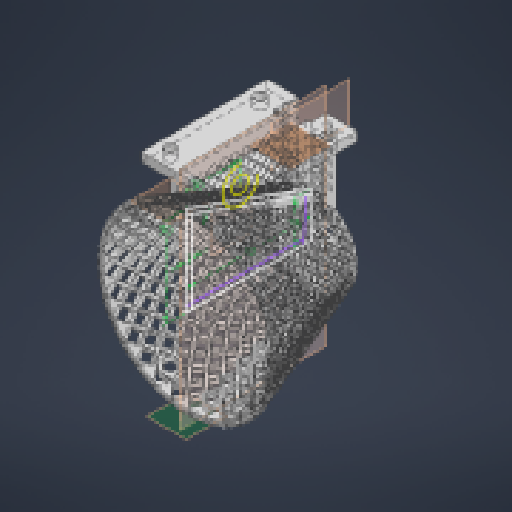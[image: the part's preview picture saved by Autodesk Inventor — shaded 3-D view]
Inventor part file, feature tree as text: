
AUTODESK INVENTOR PART (.ipt)
format: ipt  version: 2025 (Build 290162000, 162)  size: 3,707,392 bytes
history: native  units: mm
features: extrude x12, sketch x10, plane x9, other x9, reference x3, projected_geometry x2, pattern_circular x1, fillet x1
ambient origin geometry x8: Origin, YZ Plane, XZ Plane, XY Plane, X Axis, Y Axis, Z Axis, Center Point
bodies: Solid1 (feature_tree)
feature tree (47):
  plane  "Work Plane1"
  other  "hoop revolution"
  extrude  "net holes"  Depth=25.0mm
  pattern_circular  "Circular Pattern3"  Count=3  [1 undecoded]
  plane  "Work Plane15"
  extrude  "hoop slot"  TaperAngle=90.0deg  [1 undecoded]
  plane  "Work Plane10"
  extrude  "slot walls"  Depth=3.0mm
  plane  "Work Plane12"
  extrude  "arm holes"  Depth=1.0mm
  plane  "Work Plane11"
  sketch  "Sketch19"  dims[d392=1.0mm d393=1.0mm]
  plane  "Work Plane13"
  extrude  "mount holes extrusion"  Depth=1.0mm
  plane  "Work Plane16"
  extrude  "mounting holes and access holes"  Depth=1.0mm
  plane  "Work Plane18"
  extrude  "Extrusion13"  Depth=1.0mm
  plane  "Work Plane21"
  extrude  "back net reinforcement"  Depth=1.0mm
  fillet  "Fillet1"  Radius=1.0mm
  other  "middle plane for part"
  extrude  "Extrusion16"  Depth=1.0mm
  extrude  "Extrusion17"  Depth=10.0mm
  extrude  "Extrusion18"  Depth=10.0mm
  extrude  "Diameter Increase For Ball Clearance"  TaperAngle=0.0deg  [1 undecoded]
  other  "Work Axis1"
  reference  "Reference1"
  reference  "Reference2"
  reference  "Reference3"
  other  "best net sketch"
  projected_geometry  "Projected Loop3"
  sketch  "Sketch16"  dims[d387=1.0mm d388=1.0mm]
  sketch  "Sketch17"  dims[d389=1.0mm d390=1.0mm d391=1.0mm]
  projected_geometry  "Projected Loop4"
  sketch  "Sketch22"  dims[d394=1.0mm d395=1.0mm d396=1.0mm d397=0.0mm d398=0.0mm d399=3.572329mm d400=0.0mm d401=300.0mm d402=360.0deg d404=10.0mm d406=20.0mm d407=0.0mm d408=1.0mm d409=18.099mm d410=0.0mm d411=1.0mm d412=3.0mm d413=50.0mm d414=0.0mm d417=10.0mm d418=0.0mm d419=0.0mm d420=55.0mm d423=3.0mm d424=4.5mm d426=10.0mm d431=5.0mm d432=0.0mm d433=6.0mm d434=6.0mm d439=10.0mm d440=10.0mm d441=6.2mm d442=20.0mm d444=50.0mm d445=20.0mm d447=38.0mm d450=0.0mm d451=0.0mm d452=10.0mm d453=10.0mm d454=10.0mm d455=0.0mm d456=10.0mm d457=10.0mm d458=10.0mm d459=10.0mm d460=10.0mm d461=10.0mm d462=10.0mm d463=0.0mm d464=12.277724mm d465=12.278391mm d466=4.1mm d467=50.0mm d469=5.0mm d470=10.0mm d472=10.0mm d478=0.75mm d479=70.0mm d481=6.0mm d482=30.0mm d484=6.0mm d487=40.0mm d489=6.0mm d490=10.0mm d492=10.0mm d494=60.0mm d496=6.0mm d497=10.0mm d499=10.0mm d508=10.0mm d509=0.0mm d510=60.0mm d512=6.0mm d513=10.0mm d515=0.0mm d517=10.0mm d518=0.0mm d519=2.8mm d520=2.8mm d523=6.5mm d524=8.0mm d525=6.5mm d526=8.0mm d532=40.0mm d533=0.0mm d538=1.0mm d539=1.0mm d540=15.6mm d541=8.933823mm d542=1.0mm d543=0.0mm d544=0.0mm]
  sketch  "Sketch Rectangular Pattern1"  dims[d1=70.0mm d2=25.0mm d3=30.0mm]
  other  "net reinforcement"
  sketch  "Sketch Rectangular Pattern2"  dims[d5=3.0mm d6=90.0deg]
  sketch  "Sketch Rectangular Pattern3"  dims[d364=50.0mm d365=3.0mm]
  sketch  "Sketch Rectangular Pattern4"  dims[d380=1.0mm d382=1.0mm]
  sketch  "Sketch Rectangular Pattern5"  dims[d383=1.0mm d384=1.0mm]
  sketch  "Sketch Rectangular Pattern6"  dims[d385=1.0mm d386=1.0mm]
  other  "Diameter Increase"
  parser-record x1  (decoder bookkeeping rows leaked as tree rows — omitted from the tree; the rows remain in map.json)
  other  "BASKETBALL HOOP.iam"
  other  "BALL BEARING ARM:1"
note: 3 required parameter values undecoded (feature->parameter linkage not recoverable at this tier; creation-order binding heuristic only, values carry confidence <= 0.55)
note: 1 file-system path scrubbed to <path> (originals preserved in map.json)
